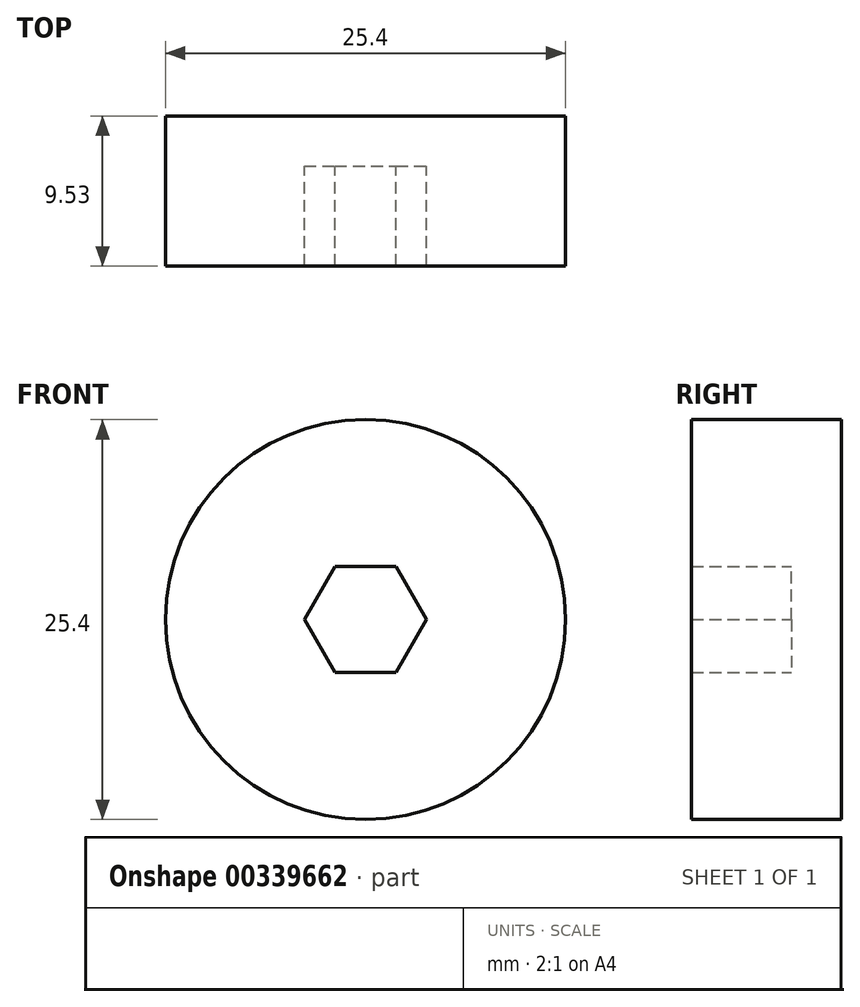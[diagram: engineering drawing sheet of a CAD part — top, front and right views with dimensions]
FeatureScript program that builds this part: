
annotation { "Feature Type Name" : "Feature", "Feature Type Description" : "" }
export const myFeature = defineFeature(function(context is Context, id is Id, definition is map)
    precondition{}
    {
        {
            var Q0;
            Q0=qCreatedBy(makeId("Front.planeOp"),FACE);
            var sketch = newSketch(context, id + "F0", { "sketchPlane" : qUnion([Q0])});
            skCircle(sketch, "E0", {"center": v(0, 0) * mm, "radius": 12.7 * mm});
            skSolve(sketch);
        }
        {
            var Q0;
            Q0=makeQuery(id+"F0.imprint","IMPRINT",FACE,{"disambiguationData":[TD([[makeQuery(id+"F0.imprint","IMPRINT",EDGE,{"derivedFrom":sQuery(id+"F0.wireOp",EDGE,"E0")}),1.0]])]});
            extrude(context, id + "F1", {"entities" : qUnion([Q0]), "oppositeDirection" : true, "depth" : 3.17 * mm});
        }
        {
            var Q0;
            Q0=makeQuery(id+"F1.opExtrude","CAP_FACE",FACE,{"disambiguationData":[OSD([sQuery(id+"F0.wireOp",EDGE,"E0")])],"isStart":true});
            var sketch = newSketch(context, id + "F2", { "sketchPlane" : qUnion([Q0])});
            skCircle(sketch, "E1.cCircle", {"center": v(0, 0) * mm, "radius": 3.37 * mm, "construction": true});
            skLineSegment(sketch, "E1.0", {"start": v(-1.94, 3.37) * mm, "end": v(1.94, 3.37) * mm});
            skLineSegment(sketch, "E1.1", {"start": v(1.94, 3.37) * mm, "end": v(3.89, 0) * mm});
            skLineSegment(sketch, "E1.2", {"start": v(3.89, 0) * mm, "end": v(1.94, -3.37) * mm});
            skLineSegment(sketch, "E1.3", {"start": v(1.94, -3.37) * mm, "end": v(-1.94, -3.37) * mm});
            skLineSegment(sketch, "E1.4", {"start": v(-1.94, -3.37) * mm, "end": v(-3.89, 0) * mm});
            skLineSegment(sketch, "E1.5", {"start": v(-3.89, 0) * mm, "end": v(-1.94, 3.37) * mm});
            skPoint(sketch, "E1.0.midPoint", {"position": v(0, 3.37) * mm});
            skSolve(sketch);
        }
        {
            var Q0;
            Q0=makeQuery(id+"F2.imprint","IMPRINT",FACE,{"disambiguationData":[TD([[makeQuery(id+"F2.imprint","IMPRINT",EDGE,{"derivedFrom":sQuery(id+"F2.wireOp",EDGE,"E1.0")}),1.0]])]});
            extrude(context, id + "F3", {"entities" : qUnion([Q0]), "operationType" : NewBodyOperationType.ADD, "depth" : 6.35 * mm});
        }
    });
